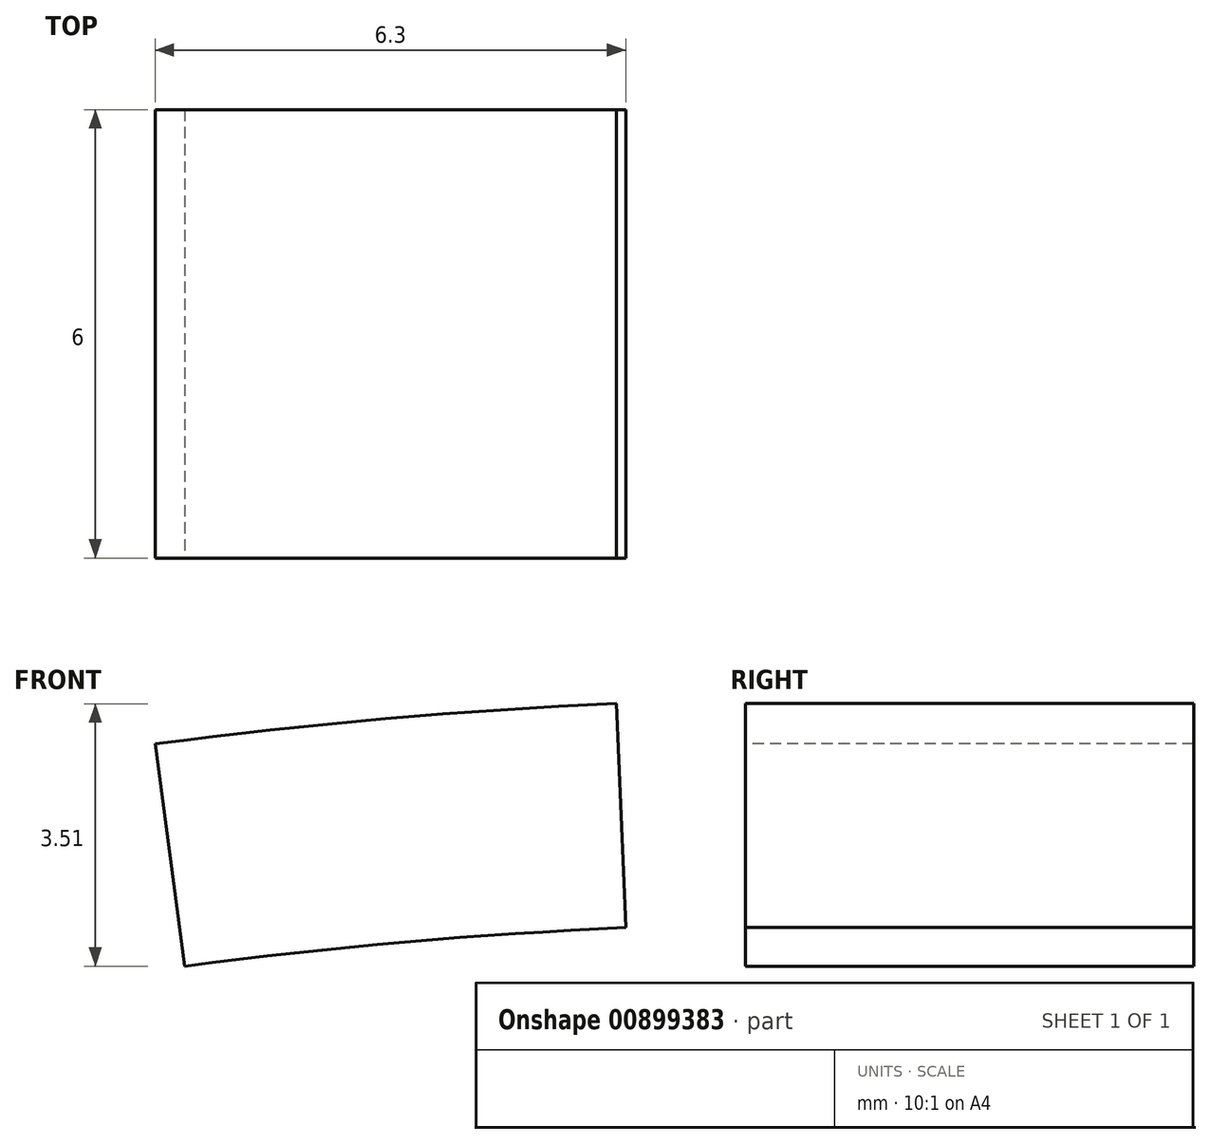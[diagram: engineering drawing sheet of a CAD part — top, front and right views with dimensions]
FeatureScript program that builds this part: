
annotation { "Feature Type Name" : "Feature", "Feature Type Description" : "" }
export const myFeature = defineFeature(function(context is Context, id is Id, definition is map)
    precondition{}
    {
        {
            var Q0;
            Q0=qCreatedBy(makeId("Front.planeOp"),FACE);
            var sketch = newSketch(context, id + "F0", { "sketchPlane" : qUnion([Q0])});
            skCircle(sketch, "E0", {"center": v(0, 0) * mm, "radius": 65 * mm});
            skCircle(sketch, "E1", {"center": v(0, 0) * mm, "radius": 71 * mm});
            skSolve(sketch);
        }
        {
            var Q0;
            Q0=makeQuery(id+"F0.imprint","IMPRINT",FACE,{"disambiguationData":[TD([[makeQuery(id+"F0.imprint","IMPRINT",EDGE,{"derivedFrom":sQuery(id+"F0.wireOp",EDGE,"E0")}),-1.0]])]});
            extrude(context, id + "F1", {"entities" : qUnion([Q0]), "depth" : 6 * mm, "offsetDistance" : 25 * mm});
        }
        {
            var Q0;
            Q0=qCreatedBy(makeId("Front.planeOp"),FACE);
            var sketch = newSketch(context, id + "F2", { "sketchPlane" : qUnion([Q0])});
            skArc(sketch, "E2", {"start": v(2.97, 67.94) * mm, "mid": v(0, 68) * mm, "end": v(-2.97, 67.94) * mm});
            skLineSegment(sketch, "E3", {"start": v(-2.97, 67.94) * mm, "end": v(-3.4, 77.93) * mm});
            skLineSegment(sketch, "E4", {"start": v(2.97, 67.94) * mm, "end": v(3.35, 76.64) * mm});
            skLineSegment(sketch, "E5", {"start": v(-2.97, 67.94) * mm, "end": v(0, 0) * mm, "construction": true});
            skLineSegment(sketch, "E6", {"start": v(2.97, 67.94) * mm, "end": v(0, 0) * mm, "construction": true});
            skLineSegment(sketch, "E7", {"start": v(-3.4, 77.93) * mm, "end": v(3.35, 76.64) * mm});
            skSolve(sketch);
        }
        {
            var Q0;
            Q0 = qSketchRegion(id + "F2", true);
            extrude(context, id + "F3", {"entities" : qUnion([Q0]), "operationType" : NewBodyOperationType.REMOVE, "depth" : 25 * mm, "offsetDistance" : 25 * mm});
        }
        {
            var Q0;
            Q0=makeQuery(id+"F1.opExtrude","CAP_FACE",FACE,{"disambiguationData":[OSD([sQuery(id+"F0.wireOp",EDGE,"E0"),sQuery(id+"F0.wireOp",EDGE,"E1")])],"isStart":false});
            var sketch = newSketch(context, id + "F4", { "sketchPlane" : qUnion([Q0])});
            skArc(sketch, "E8", {"start": v(-8.88, 67.42) * mm, "mid": v(-5.93, 67.74) * mm, "end": v(-2.97, 67.94) * mm});
            skLineSegment(sketch, "E9", {"start": v(-8.88, 67.42) * mm, "end": v(-9.27, 70.4) * mm});
            skLineSegment(sketch, "E10", {"start": v(-3.1, 70.93) * mm, "end": v(-2.97, 67.94) * mm});
            skLineSegment(sketch, "E11", {"start": v(-9.27, 70.4) * mm, "end": v(-11.22, 71.1) * mm});
            skLineSegment(sketch, "E12", {"start": v(-11.22, 71.1) * mm, "end": v(-1.85, 71.98) * mm});
            skLineSegment(sketch, "E13", {"start": v(-1.85, 71.98) * mm, "end": v(-3.1, 70.93) * mm});
            skSolve(sketch);
        }
        {
            var Q0;
            Q0=makeQuery(id+"F4.imprint","IMPRINT",FACE,{"disambiguationData":[TD([[makeQuery(id+"F4.imprint","IMPRINT",EDGE,{"derivedFrom":sQuery(id+"F4.wireOp",EDGE,"E8")}),1.0]])]});
            extrude(context, id + "F5", {"entities" : qUnion([Q0]), "operationType" : NewBodyOperationType.REMOVE, "oppositeDirection" : true, "depth" : 25 * mm, "offsetDistance" : 25 * mm});
        }
    });
